# Revit family: StorageTank_Rheem_HeavyDutyGas_Indoor_624265
name_source: partatom
category: Mechanical Equipment
units: mm (PartAtom-declared; Revit-internal decimal feet)

## family parameters
Cut with Voids When Loaded = No
Host = Face
Part Type = Normal
Room Calculation Point = No
Round Connector Dimension = Use Diameter
Shared = No

## types (2) — shared parameters
A = 1805 mm  [stored 5.92192 ft]
B = 610 mm  [stored 2.00131 ft]
C = 745 mm  [stored 2.44423 ft]
CW&PrimaryFlowDiameter = 32  [stored 0.104987 ft]
Capacity_ANZRS = 265.0 L
D = 1461 mm
Description = Rheem Heavy Duty Gas water heaters have been designed to supply large quantities of hot water. The cylinder is protected by multiple anodes and a double layer of vitreous enamel.
Diameter_ANZRS = 610 mm  [stored 2.00131 ft]
DrainDiameter = 20 mm  [stored 0.0656168 ft]
E = 711 mm
F = 340 mm
Frequency_ANZRS = 50 Hz
G = 1661 mm  [stored 5.44948 ft]
GasConnectionDiameter = 20  [stored 0.0656168 ft]
HWOutletDiameter = 32  [stored 0.104987 ft]
Height_ANZRS = 1805 mm  [stored 5.92192 ft]
K = 654 mm
M = 125 mm  [stored 0.410105 ft]
Manufacturer = Rheem
Material_ANZRS = Metal-Steel-Rheem-Galvanised
MaxStoredWaterTemperature = 82 °C
MaxWaterSupplyPressure_WithECV = 680.00 kPa
MaxWaterSupplyPressure_WithoutECV = 800.00 kPa
Model = Rheem Heavy Duty Gas 265L - Indoor
ModifiedIssue_ANZRS = 20200723.01 $
PowerFactor_ANZRS = 1
ProductCode_ANZRS = 624265
Radius = 305 mm  [stored 1.00066 ft]
T&PRValveDiameter = 20  [stored 0.0656168 ft]
URL = https://www.rheem.com.au
Voltage_ANZRS = 240 V
WeightNet_ANZRS = 137.00 kg
zero-valued in all types: Default Elevation

## per-type parameters (varying)
| type | HourlyGasConsumption | MinGasPressure | Type Comments |
| Natural Gas | 110000000 J | 1.13 kPa | 410L first hour delivery @ 50°C rise |
| Propane Gas | 100000000 J | 2.75 kPa | 380L first hour delivery @ 50°C rise |

note: [stored X ft] marks values corroborated as IEEE doubles in the binary element streams (Revit-internal decimal feet)

## geometry (parser evidence)
native form markers: Sweep x3
no freeform markers — native parametric forms only
